# Revit family: 0049289
name_source: partatom
category: Lighting Fixtures
revit_build: Autodesk Revit 2017 (Build: 20160225_1515(x64)
units: mm (PartAtom-declared; Revit-internal decimal feet)

## family parameters
Cut with Voids When Loaded = No
Host = Face
Light Source = Yes
OmniClass Number = 23.80.70.00
OmniClass Title = Lighting
Part Type = Normal
Room Calculation Point = No
Round Connector Dimension = Use Diameter
Shared = No

## types (1)
- 0049289 START Surface IP66 1100lm 840 SD BLK
    Apparent Load = 12 VA
    Assembly Code = D5020200
    AssetType = Fixed
    ClassificationName = Uniclass2015
    ClassificationValue = EF_70_80
    Color Filter = 16777215
    Cost = 0 $
    Default Elevation = 1219 mm
    Description = Sensor Dim LED exterior surface mounted luminaire, 1100lm, 12W power consumption, 92lm/W efficacy, 4000K color temperature, CRI80, IP66, IK10, 50,000 hours (L70), black housnig, vandal resistant
    Dimming Lamp Color Temperature Shift = <None>
    DocumentationLiterature = http://www.sylvania-lighting.com
    DurationUnit = hours
    ElectricShockClassification = Class II
    Emit Shape Visible in Rendering = No
    Emit from Circle Diameter = 200 mm  [stored 0.656168 ft]
    ExpectedLife = 50000
    HoleAngle_SYL = 45.00°
    HoleHoleRad_SYL = 6 mm  [stored 0.019685 ft]
    HoleRad_SYL = 134 mm
    IfcExportAs = IfcLightFixtureType
    IfcExportType = IfcLightFixtureType
    ImpactProtectionIndex = IK10
    IngressProtection = IP66
    InputNominalFrequency = 50/60 Hz
    InputVoltage = 220-240 V AC
    Keynote = 16500
    Lamp = LED
    LampColourRenderingIndex = 80
    LampColourTemperature = 4000 K
    LampNominalLuminous = 1100 lm
    LampsType = LED
    LuminousEfficacy = 92 lm/W
    Manufacturer = Feilo Sylvania
    ManufacturerName = Feilo Sylvania
    Material = pc polycarbonate housing, pc polycarbonate diffuser
    Material_1_SYL = Body-Sylvania-StartSurfaceIP66-Black
    Material_2_SYL = Diffuser-Sylvania-StartSurfaceIP66
    Material_3_SYL = LED-Sylvania-StartSurfaceIP66
    Model = START Surface IP66 1100lm 840 IK10 SensorDim BLK
    ModelNumber = 0049289
    ModelReference = START Surface IP66 1100lm 840 IK10 SensorDim BLK
    Name = START Surface IP66 1100lm 840 IK10 SensorDim BLK
    NominalDepth = 300 mm
    NominalHeight = 90 mm  [stored 0.295276 ft]
    NominalLength = 300 mm
    Photometric Web File = 0049289.ies
    PowerConsumption = 12 W
    PowerFactor = 0
    Tilt Angle = -90.00°
    Type Image = <None>
    TypeName = START Surface IP66 1100lm 840 IK10 SensorDim BLK
    URL = http://www.sylvania-lighting.com
    Voltage = 0 V
    Weight = 4.68 kg

note: [stored X ft] marks values corroborated as IEEE doubles in the binary element streams (Revit-internal decimal feet)

## geometry (parser evidence)
native form markers: Sweep x3
no freeform markers — native parametric forms only
